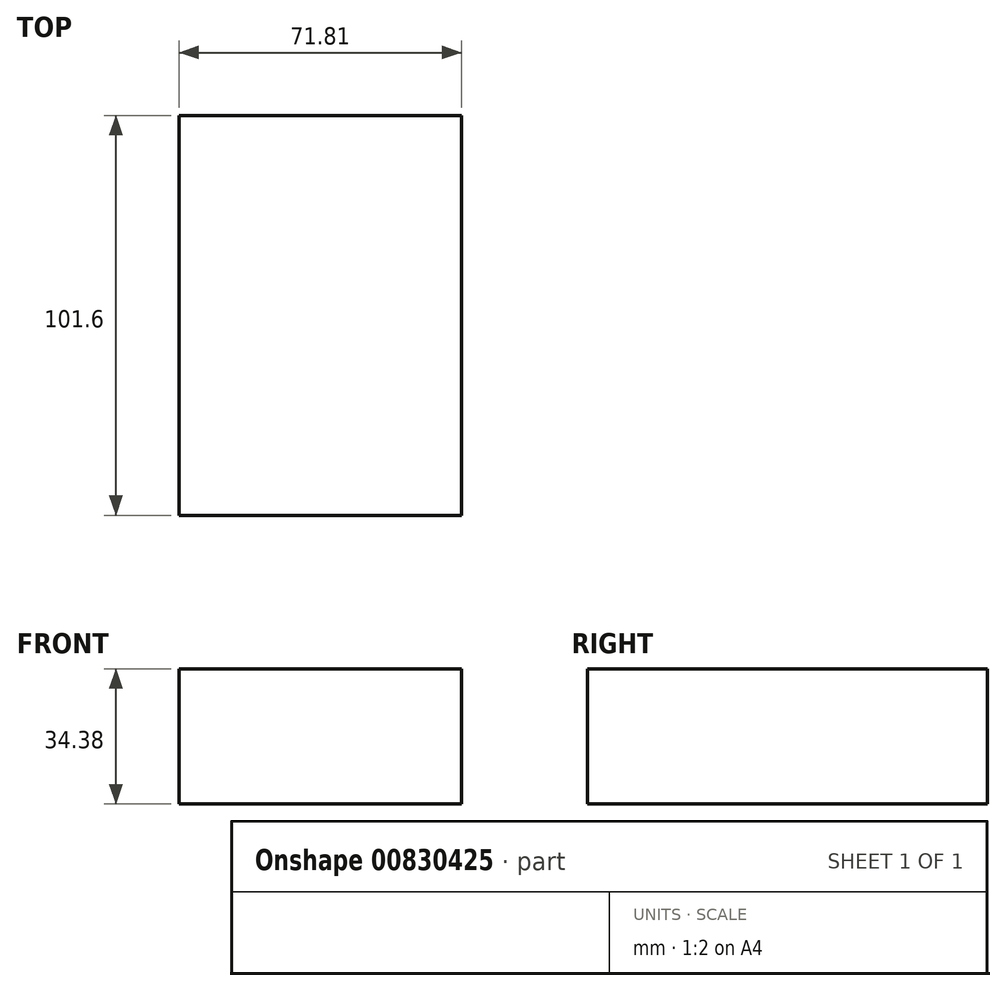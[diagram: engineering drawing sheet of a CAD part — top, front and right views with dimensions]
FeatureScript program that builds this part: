
annotation { "Feature Type Name" : "Feature", "Feature Type Description" : "" }
export const myFeature = defineFeature(function(context is Context, id is Id, definition is map)
    precondition{}
    {
        {
            var Q0;
            Q0=qCreatedBy(makeId("Front.planeOp"),FACE);
            var sketch = newSketch(context, id + "F0", { "sketchPlane" : qUnion([Q0])});
            skLineSegment(sketch, "E0.bottom", {"start": v(0, 0) * mm, "end": v(71.8, 0) * mm});
            skLineSegment(sketch, "E0.top", {"start": v(0, 34.38) * mm, "end": v(71.8, 34.38) * mm});
            skLineSegment(sketch, "E0.left", {"start": v(0, 0) * mm, "end": v(0, 34.38) * mm});
            skLineSegment(sketch, "E0.right", {"start": v(71.8, 0) * mm, "end": v(71.8, 34.38) * mm});
            skSolve(sketch);
        }
        {
            var Q0;
            Q0=makeQuery(id+"F0.imprint","IMPRINT",FACE,{"disambiguationData":[TD([[makeQuery(id+"F0.imprint","IMPRINT",EDGE,{"derivedFrom":sQuery(id+"F0.wireOp",EDGE,"E0.bottom")}),1.0]])]});
            extrude(context, id + "F1", {"entities" : qUnion([Q0]), "depth" : 101.6 * mm, "offsetDistance" : 25.4 * mm});
        }
    });
